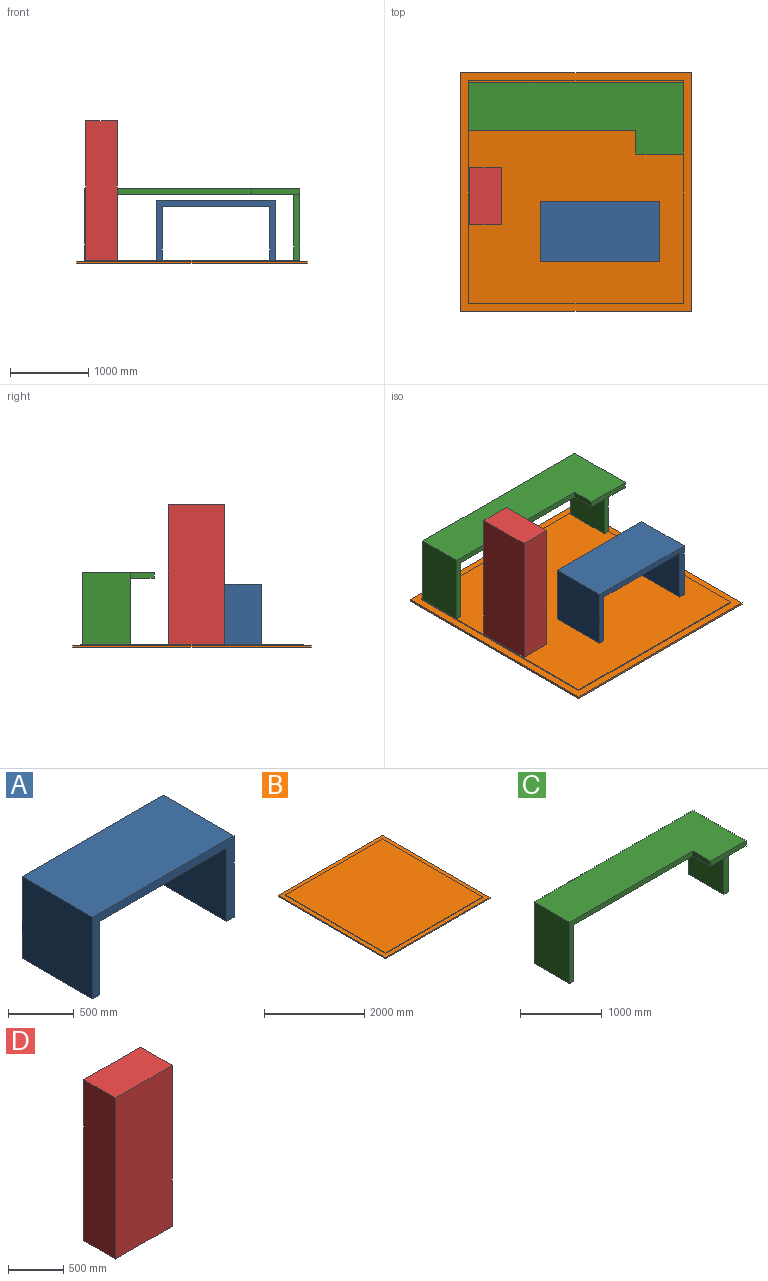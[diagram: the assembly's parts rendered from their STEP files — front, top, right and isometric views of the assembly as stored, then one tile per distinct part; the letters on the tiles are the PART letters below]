
ASSEMBLY  parts=4 mates=4
PART A: 10 faces, bbox 1524x762x762 mm
  f0: plane 762x76.2mm, normal (0,0,-1), area 58064.4mm2, adj f1,f2,f4,f8
  f1: plane 1524x762mm, normal (0,1,0), area 220644.7mm2, adj f0,f3,f4,f5,f6,f7,f8,f9
  f2: plane 1524x762mm, normal (0,-1,0), area 220644.7mm2, adj f0,f3,f4,f5,f6,f7,f8,f9
  f3: plane 762x762mm, normal (-1,0,0), area 580644mm2, adj f1,f2,f5,f6
  f4: plane 762x762mm, normal (1,0,0), area 580644mm2, adj f0,f1,f2,f5
  f5: plane 1524x762mm, normal (0,0,1), area 1161288mm2, adj f1,f2,f3,f4
  f6: plane 762x76.2mm, normal (0,0,-1), area 58064.4mm2, adj f1,f2,f3,f9
  f7: plane 1371.6x762mm, normal (0,0,-1), area 1045159.2mm2, adj f1,f2,f8,f9
  f8: plane 762x685.8mm, normal (-1,0,0), area 522579.6mm2, adj f0,f1,f2,f7
  f9: plane 762x685.8mm, normal (1,0,0), area 522579.6mm2, adj f1,f2,f6,f7
PART B: 11 faces, bbox 2946.4x3048x38.1 mm
  f0: plane 3048x2946.4mm, normal (0,0,1), area 1176771.8mm2, adj f1,f2,f3,f4,f6,f7,f8,f9
  f1: plane 3048x25.4mm, normal (1,0,0), area 77419.2mm2, adj f0,f2,f4,f5
  f2: plane 2946.4x25.4mm, normal (0,1,0), area 74838.6mm2, adj f0,f1,f3,f5
  f3: plane 3048x25.4mm, normal (-1,0,0), area 77419.2mm2, adj f0,f2,f4,f5
  f4: plane 2946.4x25.4mm, normal (0,-1,0), area 74838.6mm2, adj f0,f1,f3,f5
  f5: plane 3048x2946.4mm, normal (0,0,-1), area 8980627.2mm2, adj f1,f2,f3,f4
  f6: plane 2743.2x12.7mm, normal (0,1,0), area 34838.6mm2, adj f0,f7,f9,f10
  f7: plane 2844.8x12.7mm, normal (-1,0,0), area 36129mm2, adj f0,f6,f8,f10
  f8: plane 2743.2x12.7mm, normal (0,-1,0), area 34838.6mm2, adj f0,f7,f9,f10
  f9: plane 2844.8x12.7mm, normal (1,0,0), area 36129mm2, adj f0,f6,f8,f10
  f10: plane 2844.8x2743.2mm, normal (0,0,1), area 7803855.4mm2, adj f6,f7,f8,f9
PART C: 13 faces, bbox 2743.2x914.4x914.4 mm
  f0: plane 2133.6x914.4mm, normal (0,-1,0), area 226451.2mm2, adj f1,f3,f6,f8,f9,f11
  f1: plane 609.6x76.2mm, normal (0,0,-1), area 46451.5mm2, adj f0,f3,f5,f9
  f2: plane 838.2x76.2mm, normal (0,-1,0), area 63870.8mm2, adj f4,f7,f8,f10
  f3: plane 914.4x609.6mm, normal (-1,0,0), area 557418.2mm2, adj f0,f1,f5,f6
  f4: plane 914.4x914.4mm, normal (1,0,0), area 580644mm2, adj f2,f5,f6,f7,f8,f12
  f5: plane 2743.2x914.4mm, normal (0,1,0), area 336773.5mm2, adj f1,f3,f4,f6,f7,f8,f9,f10
  f6: plane 2743.2x914.4mm, normal (0,0,1), area 1858060.8mm2, adj f0,f3,f4,f5,f11,f12
  f7: plane 609.6x76.2mm, normal (0,0,-1), area 46451.5mm2, adj f2,f4,f5,f10
  f8: plane 2667x914.4mm, normal (0,0,-1), area 1765157.8mm2, adj f0,f2,f4,f5,f9,f10,f11,f12
  f9: plane 838.2x609.6mm, normal (1,0,0), area 510966.7mm2, adj f0,f1,f5,f8
  f10: plane 838.2x609.6mm, normal (-1,0,0), area 510966.7mm2, adj f2,f5,f7,f8
  f11: plane 304.8x76.2mm, normal (-1,0,0), area 23225.8mm2, adj f0,f6,f8,f12
  f12: plane 609.6x76.2mm, normal (0,-1,0), area 46451.5mm2, adj f4,f6,f8,f11
PART D: 6 faces, bbox 723.9x406.4x1778 mm
  f0: plane 1778x723.9mm, normal (0,1,0), area 1287094.2mm2, adj f1,f3,f4,f5
  f1: plane 1778x406.4mm, normal (-1,0,0), area 722579.2mm2, adj f0,f2,f4,f5
  f2: plane 1778x723.9mm, normal (0,-1,0), area 1287094.2mm2, adj f1,f3,f4,f5
  f3: plane 1778x406.4mm, normal (1,0,0), area 722579.2mm2, adj f0,f2,f4,f5
  f4: plane 723.9x406.4mm, normal (0,0,1), area 294193mm2, adj f0,f1,f2,f3
  f5: plane 723.9x406.4mm, normal (0,0,-1), area 294193mm2, adj f0,f1,f2,f3
PLACE A t=(822.07,-82.69,874.16)mm
PLACE B t=(-91.84,-61.09,874.16)mm fixed
PLACE C t=(-89.66,-85.8,874.16)mm
PLACE D rot(axis=(0,0,-1),90deg) t=(-318.24,344.49,874.16)mm
MATE planar B.f10 <-> D.f5  axis (0,0,1) through (-91.84,-61.09,912.26)mm
MATE parallel B.f3 <-> D.f2  axis (-1,0,0) through (-1565.04,-61.09,886.86)mm
MATE planar C.f1 <-> B.f10  axis (0,0,-1) through (-1423.16,1031.8,912.26)mm
MATE planar A.f6 <-> B.f10  axis (0,0,-1) through (-511.43,-565.29,912.26)mm
